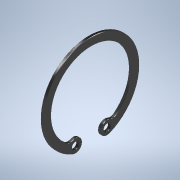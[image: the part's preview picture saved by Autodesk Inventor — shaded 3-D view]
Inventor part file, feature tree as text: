
AUTODESK INVENTOR PART (.ipt)
format: ipt  version: 2020.2 (Build 242310000, 310)  size: 175,616 bytes
history: native  units: mm
features: other x1, extrude x1, chamfer x1, sketch x1
ambient origin geometry x8: Origin, YZ Plane, XZ Plane, XY Plane, X Axis, Y Axis, Z Axis, Center Point
bodies: Body1 (feature_tree)
feature tree (4):
  other  "Bryła1"
  extrude  "Wyciągnięcie proste1"  Depth=18.0mm
  chamfer  "Faza1"  Distance=15.0mm
  sketch  "Szkic1"
